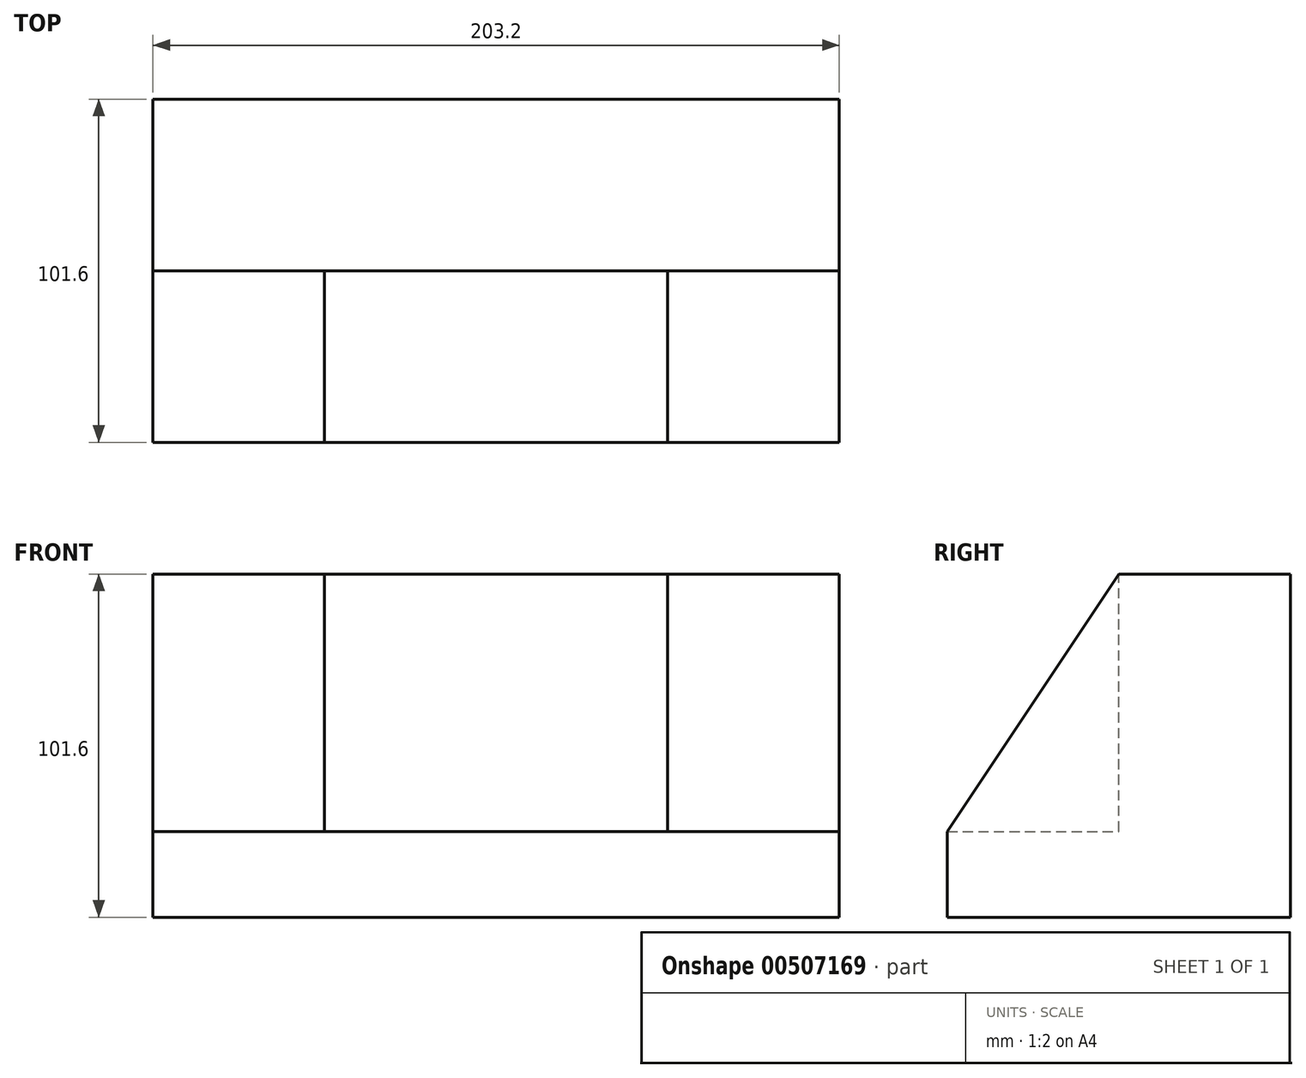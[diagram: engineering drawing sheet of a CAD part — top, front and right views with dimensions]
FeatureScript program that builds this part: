
annotation { "Feature Type Name" : "Feature", "Feature Type Description" : "" }
export const myFeature = defineFeature(function(context is Context, id is Id, definition is map)
    precondition{}
    {
        {
            var Q0;
            Q0=qCreatedBy(makeId("Front.planeOp"),FACE);
            var sketch = newSketch(context, id + "F0", { "sketchPlane" : qUnion([Q0])});
            skLineSegment(sketch, "E0.bottom", {"start": v(-101.6, 50.8) * mm, "end": v(101.6, 50.8) * mm});
            skLineSegment(sketch, "E0.top", {"start": v(-101.6, -50.8) * mm, "end": v(101.6, -50.8) * mm});
            skLineSegment(sketch, "E0.left", {"start": v(-101.6, 50.8) * mm, "end": v(-101.6, -50.8) * mm});
            skLineSegment(sketch, "E0.right", {"start": v(101.6, 50.8) * mm, "end": v(101.6, -50.8) * mm});
            skSolve(sketch);
        }
        {
            var Q0;
            Q0=qSketchRegion(id+"F0",true);
            extrude(context, id + "F1", {"entities" : qUnion([Q0]), "depth" : 101.6 * mm});
        }
        {
            var Q0;
            Q0=makeQuery(id+"F1.opExtrude","SWEPT_FACE",FACE,{"disambiguationData":[OSD([sQuery(id+"F0.wireOp",EDGE,"E0.bottom")])]});
            var sketch = newSketch(context, id + "F2", { "sketchPlane" : qUnion([Q0])});
            skLineSegment(sketch, "E1.bottom", {"start": v(-50.8, -101.6) * mm, "end": v(50.8, -101.6) * mm});
            skLineSegment(sketch, "E1.top", {"start": v(-50.8, -50.8) * mm, "end": v(50.8, -50.8) * mm});
            skLineSegment(sketch, "E1.left", {"start": v(-50.8, -101.6) * mm, "end": v(-50.8, -50.8) * mm});
            skLineSegment(sketch, "E1.right", {"start": v(50.8, -101.6) * mm, "end": v(50.8, -50.8) * mm});
            skSolve(sketch);
        }
        {
            var Q0;
            Q0 = qSketchRegion(id + "F2", true);
            extrude(context, id + "F3", {"entities" : qUnion([Q0]), "operationType" : NewBodyOperationType.REMOVE, "oppositeDirection" : true, "depth" : 76.2 * mm});
        }
        {
            var Q0;
            {var subQ0=sQuery(id+"F0.wireOp",EDGE,"E0.bottom");var subQ1=sQuery(id+"F0.wireOp",EDGE,"E0.left");Q0=makeQuery(id+"F3.boolean.opBoolean","SPLIT",EDGE,{"disambiguationData":[TD([makeQuery(id+"F1.opExtrude","SWEPT_FACE",FACE,{"disambiguationData":[OSD([subQ1])]})])],"derivedFrom":makeQuery(id+"F1.opExtrude","CAP_EDGE",EDGE,{"disambiguationData":[OSD([subQ0])],"isStart":false})});}
            chamfer(context, id + "F4", {"entities" : qUnion([Q0]), "chamferType" : ChamferType.TWO_OFFSETS, "width1" : 50.8 * mm, "oppositeDirection" : false, "width2" : 76.2 * mm, "tangentPropagation" : true});
        }
        {
            var Q0;
            {var subQ0=sQuery(id+"F0.wireOp",EDGE,"E0.bottom");var subQ1=sQuery(id+"F0.wireOp",EDGE,"E0.right");Q0=makeQuery(id+"F3.boolean.opBoolean","SPLIT",EDGE,{"disambiguationData":[TD([makeQuery(id+"F1.opExtrude","SWEPT_FACE",FACE,{"disambiguationData":[OSD([subQ1])]})])],"derivedFrom":makeQuery(id+"F1.opExtrude","CAP_EDGE",EDGE,{"disambiguationData":[OSD([subQ0])],"isStart":false})});}
            chamfer(context, id + "F5", {"entities" : qUnion([Q0]), "chamferType" : ChamferType.TWO_OFFSETS, "width1" : 50.8 * mm, "oppositeDirection" : false, "width2" : 76.2 * mm, "tangentPropagation" : true});
        }
    });
